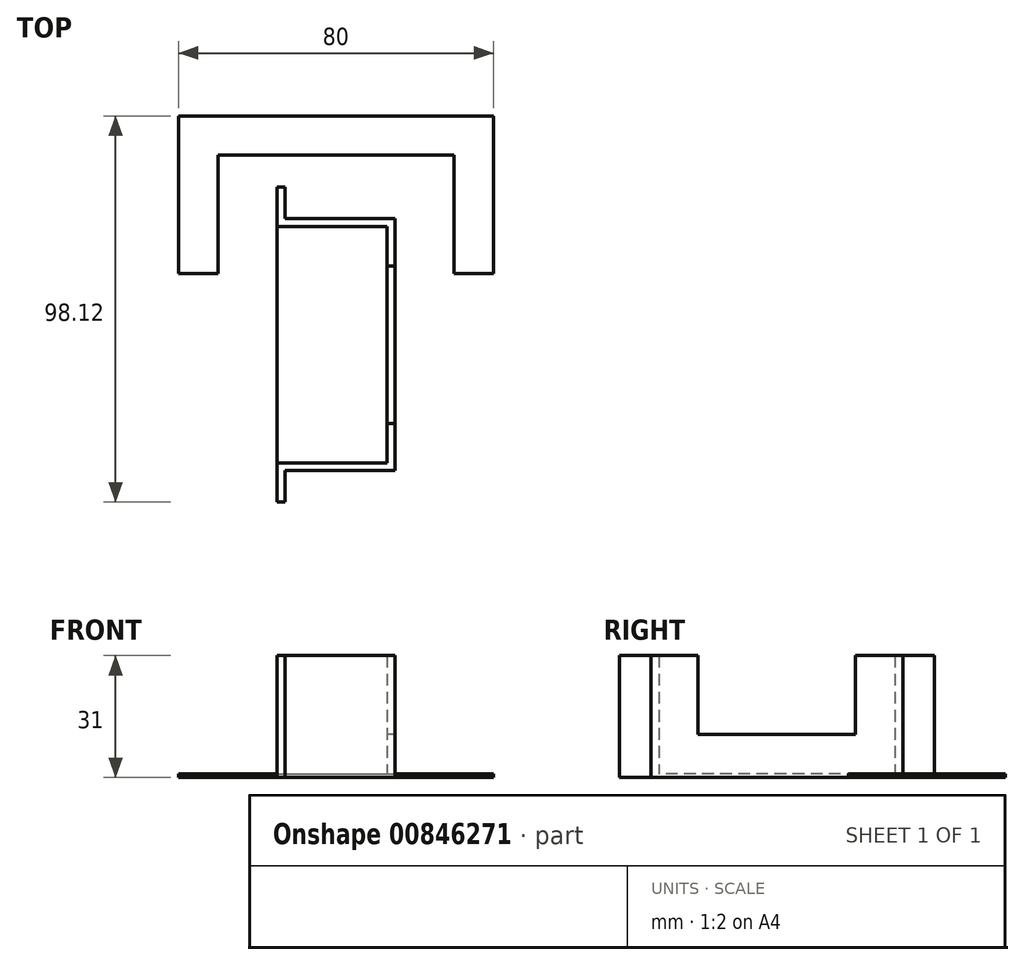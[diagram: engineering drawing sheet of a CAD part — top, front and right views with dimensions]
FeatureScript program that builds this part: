
annotation { "Feature Type Name" : "Feature", "Feature Type Description" : "" }
export const myFeature = defineFeature(function(context is Context, id is Id, definition is map)
    precondition{}
    {
        {
            var Q0;
            Q0=qCreatedBy(makeId("Top.planeOp"),FACE);
            var sketch = newSketch(context, id + "F0", { "sketchPlane" : qUnion([Q0])});
            skLineSegment(sketch, "E0.bottom", {"start": v(-15, 32) * mm, "end": v(15, 32) * mm});
            skLineSegment(sketch, "E0.top", {"start": v(-15, -32) * mm, "end": v(15, -32) * mm});
            skLineSegment(sketch, "E0.left", {"start": v(-15, 32) * mm, "end": v(-15, -32) * mm});
            skPoint(sketch, "E0.middle", {"position": v(0, 0) * mm});
            skLineSegment(sketch, "E1", {"start": v(-15, 30) * mm, "end": v(13, 30) * mm});
            skLineSegment(sketch, "E2", {"start": v(13, -30) * mm, "end": v(-15, -30) * mm});
            skLineSegment(sketch, "E3", {"start": v(-15, -32) * mm, "end": v(-15, -40) * mm});
            skLineSegment(sketch, "E4", {"start": v(-15, -40) * mm, "end": v(-13, -40) * mm});
            skLineSegment(sketch, "E5", {"start": v(-13, -40) * mm, "end": v(-13, -32) * mm});
            skLineSegment(sketch, "E6", {"start": v(-15, 32) * mm, "end": v(-15, 40) * mm});
            skLineSegment(sketch, "E7", {"start": v(-15, 40) * mm, "end": v(-13, 40) * mm});
            skLineSegment(sketch, "E8", {"start": v(-13, 40) * mm, "end": v(-13, 32) * mm});
            skLineSegment(sketch, "E9", {"start": v(13, 30) * mm, "end": v(13, 20) * mm});
            skLineSegment(sketch, "E10", {"start": v(13, 20) * mm, "end": v(15, 20) * mm});
            skLineSegment(sketch, "E11", {"start": v(15, 20) * mm, "end": v(15, 32) * mm});
            skLineSegment(sketch, "E12", {"start": v(15, -32) * mm, "end": v(15, -20) * mm});
            skLineSegment(sketch, "E13", {"start": v(15, -20) * mm, "end": v(13, -20) * mm});
            skLineSegment(sketch, "E14", {"start": v(13, -20) * mm, "end": v(13, -30) * mm});
            skLineSegment(sketch, "E15", {"start": v(15, 20) * mm, "end": v(15, -20) * mm});
            skLineSegment(sketch, "E16", {"start": v(13, 20) * mm, "end": v(13, -20) * mm});
            skSolve(sketch);
        }
        {
            var Q0;
            Q0=makeQuery(id+"F0.imprint","IMPRINT",FACE,{"disambiguationData":[TD([[makeQuery(id+"F0.imprint","IMPRINT",EDGE,{"derivedFrom":sQuery(id+"F0.wireOp",EDGE,"E10")}),-1.0]])]});
            extrude(context, id + "F1", {"entities" : qUnion([Q0]), "depth" : 11 * mm, "offsetDistance" : 25 * mm});
        }
        {
            var Q0;
            {var subQ0=sQuery(id+"F0.wireOp",EDGE,"E6");Q0=makeQuery(id+"F0.imprint","IMPRINT",FACE,{"disambiguationData":[TD([[makeQuery(id+"F0.imprint","IMPRINT",EDGE,{"derivedFrom":subQ0}),-1.0]])]});}
            var Q1;
            {var subQ0=sQuery(id+"F0.wireOp",EDGE,"E1");Q1=makeQuery(id+"F0.imprint","IMPRINT",FACE,{"disambiguationData":[TD([[makeQuery(id+"F0.imprint","IMPRINT",EDGE,{"derivedFrom":subQ0}),1.0]])]});}
            var Q2;
            {var subQ3=sQuery(id+"F0.wireOp",EDGE,"E2");Q2=makeQuery(id+"F0.imprint","IMPRINT",FACE,{"disambiguationData":[TD([[makeQuery(id+"F0.imprint","IMPRINT",EDGE,{"derivedFrom":subQ3}),1.0]])]});}
            var Q3;
            {var subQ0=sQuery(id+"F0.wireOp",EDGE,"E3");Q3=makeQuery(id+"F0.imprint","IMPRINT",FACE,{"disambiguationData":[TD([[makeQuery(id+"F0.imprint","IMPRINT",EDGE,{"derivedFrom":subQ0}),1.0]])]});}
            extrude(context, id + "F2", {"entities" : qUnion([Q0, Q1, Q2, Q3]), "operationType" : NewBodyOperationType.ADD, "depth" : 31 * mm, "offsetDistance" : 25 * mm});
        }
        {
            var Q0;
            {var subQ1=sQuery(id+"F0.wireOp",EDGE,"E1");Q0=makeQuery(id+"F0.imprint","IMPRINT",FACE,{"disambiguationData":[TD([[makeQuery(id+"F0.imprint","IMPRINT",EDGE,{"derivedFrom":subQ1}),-1.0]])]});}
            extrude(context, id + "F3", {"entities" : qUnion([Q0]), "operationType" : NewBodyOperationType.ADD, "depth" : 1 * mm, "offsetDistance" : 25 * mm});
        }
        {
            var Q0;
            Q0=qCreatedBy(makeId("Top.planeOp"),FACE);
            var sketch = newSketch(context, id + "F4", { "sketchPlane" : qUnion([Q0])});
            skLineSegment(sketch, "E17.bottom", {"start": v(-40, 18.12) * mm, "end": v(40, 18.12) * mm});
            skLineSegment(sketch, "E17.top", {"start": v(-40, 58.12) * mm, "end": v(40, 58.12) * mm});
            skLineSegment(sketch, "E17.left", {"start": v(-40, 18.12) * mm, "end": v(-40, 58.12) * mm});
            skLineSegment(sketch, "E17.right", {"start": v(40, 18.12) * mm, "end": v(40, 58.12) * mm});
            skLineSegment(sketch, "E18", {"start": v(-30, 18.12) * mm, "end": v(-30, 48.12) * mm});
            skLineSegment(sketch, "E19", {"start": v(-30, 48.12) * mm, "end": v(30, 48.12) * mm});
            skLineSegment(sketch, "E20", {"start": v(30, 48.12) * mm, "end": v(30, 18.12) * mm});
            skSolve(sketch);
        }
        {
            var Q0;
            Q0=makeQuery(id+"F4.imprint","IMPRINT",FACE,{"disambiguationData":[TD([[makeQuery(id+"F4.imprint","IMPRINT",EDGE,{"derivedFrom":sQuery(id+"F4.wireOp",EDGE,"E17.top")}),-1.0]])]});
            extrude(context, id + "F5", {"entities" : qUnion([Q0]), "depth" : 1 * mm, "offsetDistance" : 25 * mm});
        }
    });
